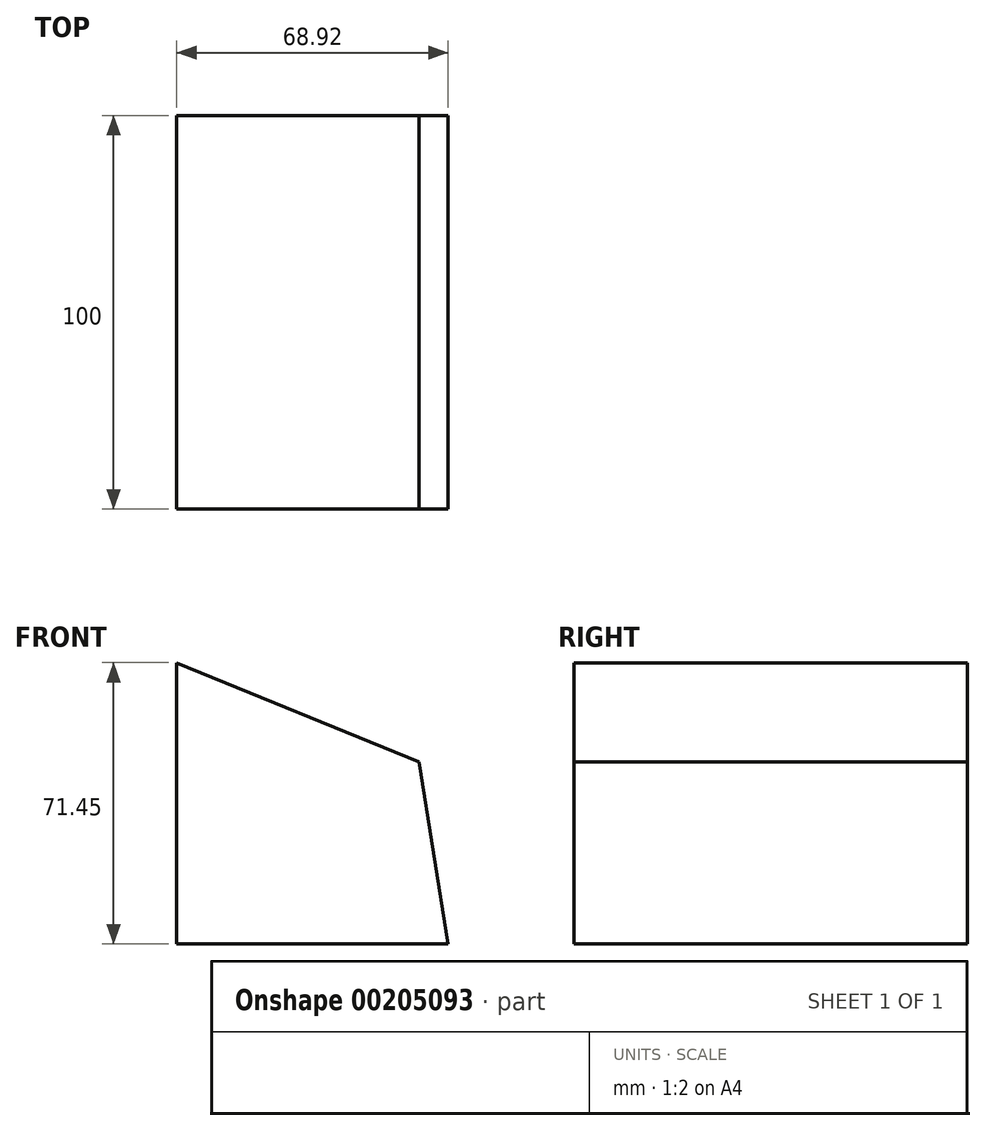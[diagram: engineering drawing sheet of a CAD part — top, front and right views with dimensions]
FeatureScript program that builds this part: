
annotation { "Feature Type Name" : "Feature", "Feature Type Description" : "" }
export const myFeature = defineFeature(function(context is Context, id is Id, definition is map)
    precondition{}
    {
        {
            var Q0;
            Q0=qCreatedBy(makeId("Front.planeOp"),FACE);
            var sketch = newSketch(context, id + "F0", { "sketchPlane" : qUnion([Q0])});
            skLineSegment(sketch, "E0", {"start": v(0, 0) * mm, "end": v(0, 71.45) * mm});
            skLineSegment(sketch, "E1", {"start": v(0, 71.45) * mm, "end": v(61.57, 46.18) * mm});
            skLineSegment(sketch, "E2", {"start": v(61.57, 46.18) * mm, "end": v(68.92, 0) * mm});
            skLineSegment(sketch, "E3", {"start": v(68.92, 0) * mm, "end": v(0, 0) * mm});
            skSolve(sketch);
        }
        {
            var Q0;
            Q0 = qSketchRegion(id + "F0", true);
            extrude(context, id + "F1", {"entities" : qUnion([Q0]), "depth" : 100 * mm});
        }
    });
